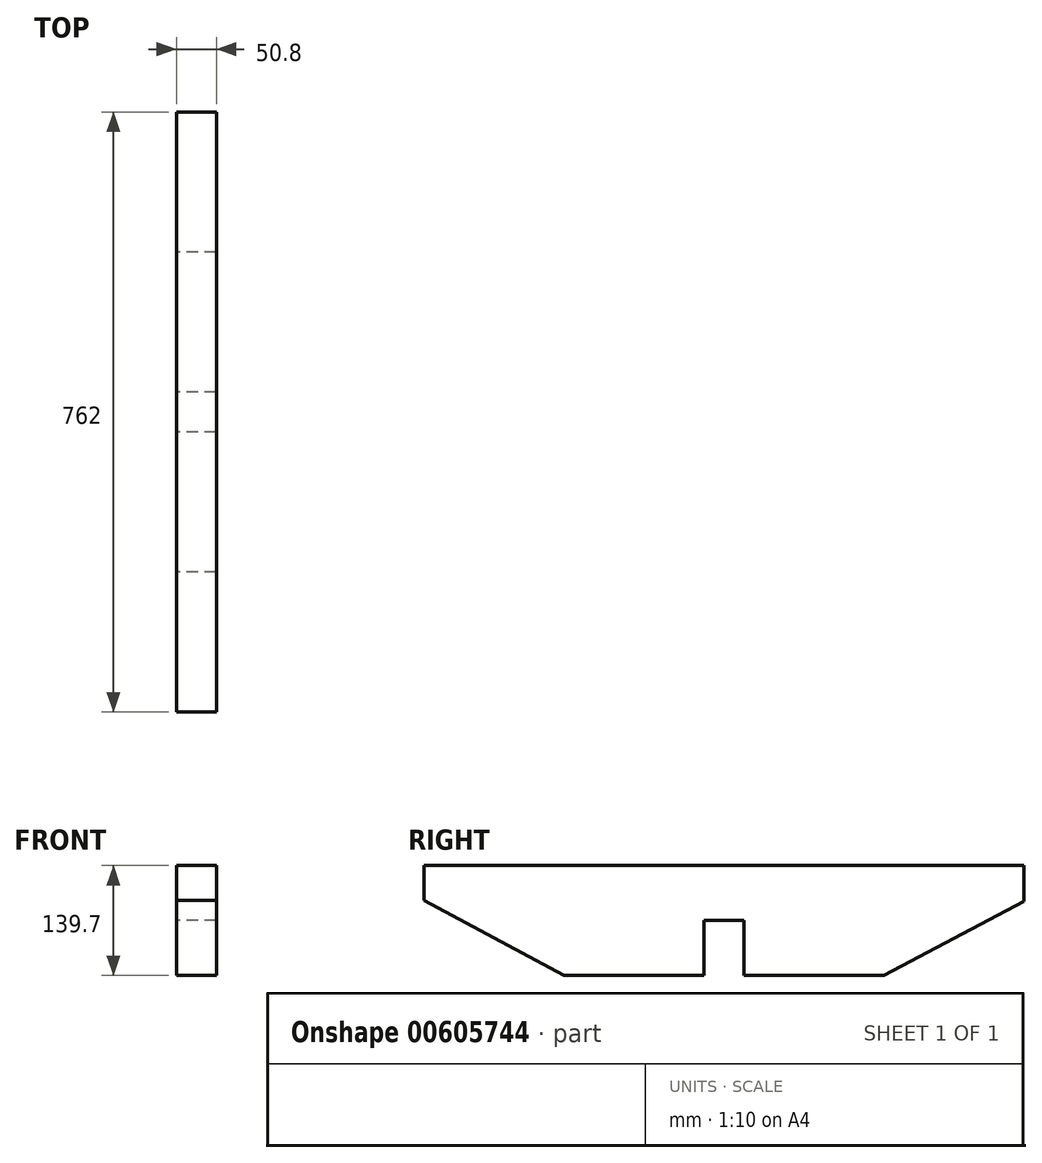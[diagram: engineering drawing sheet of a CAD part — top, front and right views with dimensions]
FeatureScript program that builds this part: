
annotation { "Feature Type Name" : "Feature", "Feature Type Description" : "" }
export const myFeature = defineFeature(function(context is Context, id is Id, definition is map)
    precondition{}
    {
        {
            var Q0;
            Q0=qCreatedBy(makeId("Right.planeOp"),FACE);
            var sketch = newSketch(context, id + "F0", { "sketchPlane" : qUnion([Q0])});
            skLineSegment(sketch, "E0.bottom", {"start": v(0, -27.12) * mm, "end": v(-177.8, -27.12) * mm});
            skLineSegment(sketch, "E0.top", {"start": v(0, 112.58) * mm, "end": v(-355.6, 112.58) * mm});
            skLineSegment(sketch, "E0.left", {"start": v(0, -27.12) * mm, "end": v(0, 112.58) * mm});
            skLineSegment(sketch, "E0.right", {"start": v(-355.6, 67.94) * mm, "end": v(-355.6, 112.58) * mm});
            skPoint(sketch, "E0.middle", {"position": v(-177.8, 42.73) * mm});
            skLineSegment(sketch, "E1.bottom", {"start": v(50.8, 112.58) * mm, "end": v(406.4, 112.58) * mm});
            skLineSegment(sketch, "E1.top", {"start": v(50.8, -27.12) * mm, "end": v(228.6, -27.12) * mm});
            skLineSegment(sketch, "E1.left", {"start": v(50.8, 112.58) * mm, "end": v(50.8, -27.12) * mm});
            skLineSegment(sketch, "E1.right", {"start": v(406.4, 112.58) * mm, "end": v(406.4, 66.99) * mm});
            skPoint(sketch, "E1.middle", {"position": v(228.6, 42.73) * mm});
            skLineSegment(sketch, "E2.bottom", {"start": v(0, 112.58) * mm, "end": v(50.8, 112.58) * mm});
            skLineSegment(sketch, "E2.top", {"start": v(0, 42.73) * mm, "end": v(50.8, 42.73) * mm});
            skLineSegment(sketch, "E2.left", {"start": v(0, 112.58) * mm, "end": v(0, 42.73) * mm});
            skLineSegment(sketch, "E2.right", {"start": v(50.8, 112.58) * mm, "end": v(50.8, 42.73) * mm});
            skLineSegment(sketch, "E3", {"start": v(406.4, 66.99) * mm, "end": v(228.6, -27.12) * mm});
            skLineSegment(sketch, "E4", {"start": v(-355.6, 67.94) * mm, "end": v(-177.8, -27.12) * mm});
            skPoint(sketch, "E5.orphan", {"position": v(-355.6, -27.12) * mm});
            skPoint(sketch, "E6.orphan", {"position": v(406.4, -27.12) * mm});
            skSolve(sketch);
        }
        {
            var Q0;
            Q0 = qSketchRegion(id + "F0", true);
            extrude(context, id + "F1", {"entities" : qUnion([Q0]), "depth" : 50.8 * mm, "offsetDistance" : 25.4 * mm});
        }
    });
